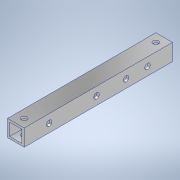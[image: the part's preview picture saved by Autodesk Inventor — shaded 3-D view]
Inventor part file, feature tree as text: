
AUTODESK INVENTOR PART (.ipt)
format: ipt  version: 2020.3 (Build 243373000, 373)  size: 188,928 bytes
history: native  units: mm
features: sketch x5, hole x4, other x1, extrude x1
ambient origin geometry x8: Origin, YZ Plane, XZ Plane, XY Plane, X Axis, Y Axis, Z Axis, Center Point
bodies: Body1 (feature_tree)
feature tree (11):
  other  "ソリッド1"
  extrude  "押し出し1"  Depth=9.0mm
  hole  "穴1"  [1 undecoded]
  hole  "穴2"  [1 undecoded]
  hole  "穴3"  [1 undecoded]
  hole  "穴4"  [1 undecoded]
  sketch  "スケッチ1"
  sketch  "スケッチ2"
  sketch  "スケッチ3"
  sketch  "スケッチ4"
  sketch  "スケッチ5"
note: 4 required parameter values undecoded (feature->parameter linkage not recoverable at this tier; creation-order binding heuristic only, values carry confidence <= 0.55)
